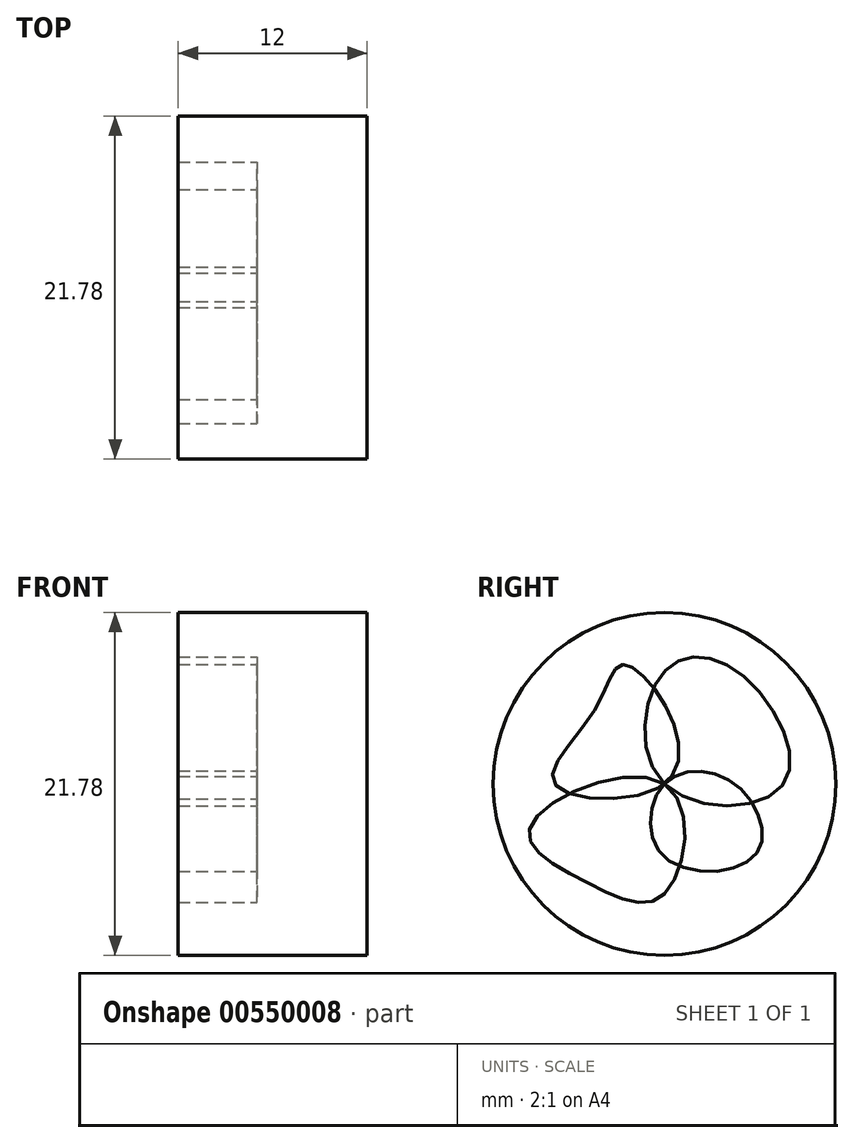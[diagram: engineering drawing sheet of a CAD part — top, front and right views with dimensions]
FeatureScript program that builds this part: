
annotation { "Feature Type Name" : "Feature", "Feature Type Description" : "" }
export const myFeature = defineFeature(function(context is Context, id is Id, definition is map)
    precondition{}
    {
        {
            var Q0;
            Q0=qCreatedBy(makeId("Right.planeOp"),FACE);
            var sketch = newSketch(context, id + "F0", { "sketchPlane" : qUnion([Q0])});
            skCircle(sketch, "E0", {"center": v(0, 0) * mm, "radius": 10.89 * mm});
            skSolve(sketch);
        }
        {
            var Q0;
            Q0=makeQuery(id+"F0.imprint","IMPRINT",FACE,{"disambiguationData":[TD([[makeQuery(id+"F0.imprint","IMPRINT",EDGE,{"derivedFrom":sQuery(id+"F0.wireOp",EDGE,"E0")}),1.0]])]});
            var sketch = newSketch(context, id + "F1", { "sketchPlane" : qUnion([Q0])});
            skFitSpline(sketch, "E1", {"points": [v(-4.46, 4.66) * mm, v(-2.72, 7.56) * mm, v(0, 5.04) * mm, v(0, 0) * mm, v(-6.98, 0) * mm, v(-4.46, 4.66) * mm]});
            skSolve(sketch);
        }
        {
            var Q0;
            Q0=makeQuery(id+"F0.imprint","IMPRINT",FACE,{"disambiguationData":[TD([[makeQuery(id+"F0.imprint","IMPRINT",EDGE,{"derivedFrom":sQuery(id+"F0.wireOp",EDGE,"E0")}),1.0]])]});
            var sketch = newSketch(context, id + "F2", { "sketchPlane" : qUnion([Q0])});
            skFitSpline(sketch, "E2", {"points": [v(0, 0) * mm, v(4.46, 0) * mm, v(5.82, -4.46) * mm, v(0, -4.66) * mm, v(0, 0) * mm]});
            skSolve(sketch);
        }
        {
            var Q0;
            Q0=makeQuery(id+"F0.imprint","IMPRINT",FACE,{"disambiguationData":[TD([[makeQuery(id+"F0.imprint","IMPRINT",EDGE,{"derivedFrom":sQuery(id+"F0.wireOp",EDGE,"E0")}),1.0]])]});
            var sketch = newSketch(context, id + "F3", { "sketchPlane" : qUnion([Q0])});
            skFitSpline(sketch, "E3", {"points": [v(0, 0) * mm, v(-8.53, -2.72) * mm, v(-5.04, -6.2) * mm, v(0, -6.98) * mm, v(0, 0) * mm]});
            skSolve(sketch);
        }
        {
            var Q0;
            Q0=makeQuery(id+"F0.imprint","IMPRINT",FACE,{"disambiguationData":[TD([[makeQuery(id+"F0.imprint","IMPRINT",EDGE,{"derivedFrom":sQuery(id+"F0.wireOp",EDGE,"E0")}),1.0]])]});
            var sketch = newSketch(context, id + "F4", { "sketchPlane" : qUnion([Q0])});
            skFitSpline(sketch, "E4", {"points": [v(0, 0) * mm, v(0, 7.18) * mm, v(4.85, 6.98) * mm, v(7.56, 0) * mm, v(0, 0) * mm]});
            skSolve(sketch);
        }
        {
            var Q0;
            Q0=sQuery(id+"F0.wireOp",EDGE,"E0");
            extrude(context, id + "F5", {"bodyType" : ToolBodyType.SURFACE, "surfaceEntities" : qUnion([Q0]), "depth" : 12 * mm, "offsetDistance" : 25 * mm});
        }
        {
            var Q0;
            Q0=sQuery(id+"F4.wireOp",EDGE,"E4");
            extrude(context, id + "F6", {"bodyType" : ToolBodyType.SURFACE, "surfaceEntities" : qUnion([Q0]), "depth" : 5 * mm, "offsetDistance" : 25 * mm});
        }
        {
            var Q0;
            Q0=sQuery(id+"F3.wireOp",EDGE,"E3");
            extrude(context, id + "F7", {"bodyType" : ToolBodyType.SURFACE, "surfaceEntities" : qUnion([Q0]), "depth" : 5 * mm, "offsetDistance" : 25 * mm});
        }
        {
            var Q0;
            Q0=sQuery(id+"F1.wireOp",EDGE,"E1");
            extrude(context, id + "F8", {"bodyType" : ToolBodyType.SURFACE, "surfaceEntities" : qUnion([Q0]), "depth" : 5 * mm, "offsetDistance" : 25 * mm});
        }
        {
            var Q0;
            Q0=sQuery(id+"F2.wireOp",EDGE,"E2");
            extrude(context, id + "F9", {"bodyType" : ToolBodyType.SURFACE, "surfaceEntities" : qUnion([Q0]), "depth" : 5 * mm, "offsetDistance" : 25 * mm});
        }
    });
